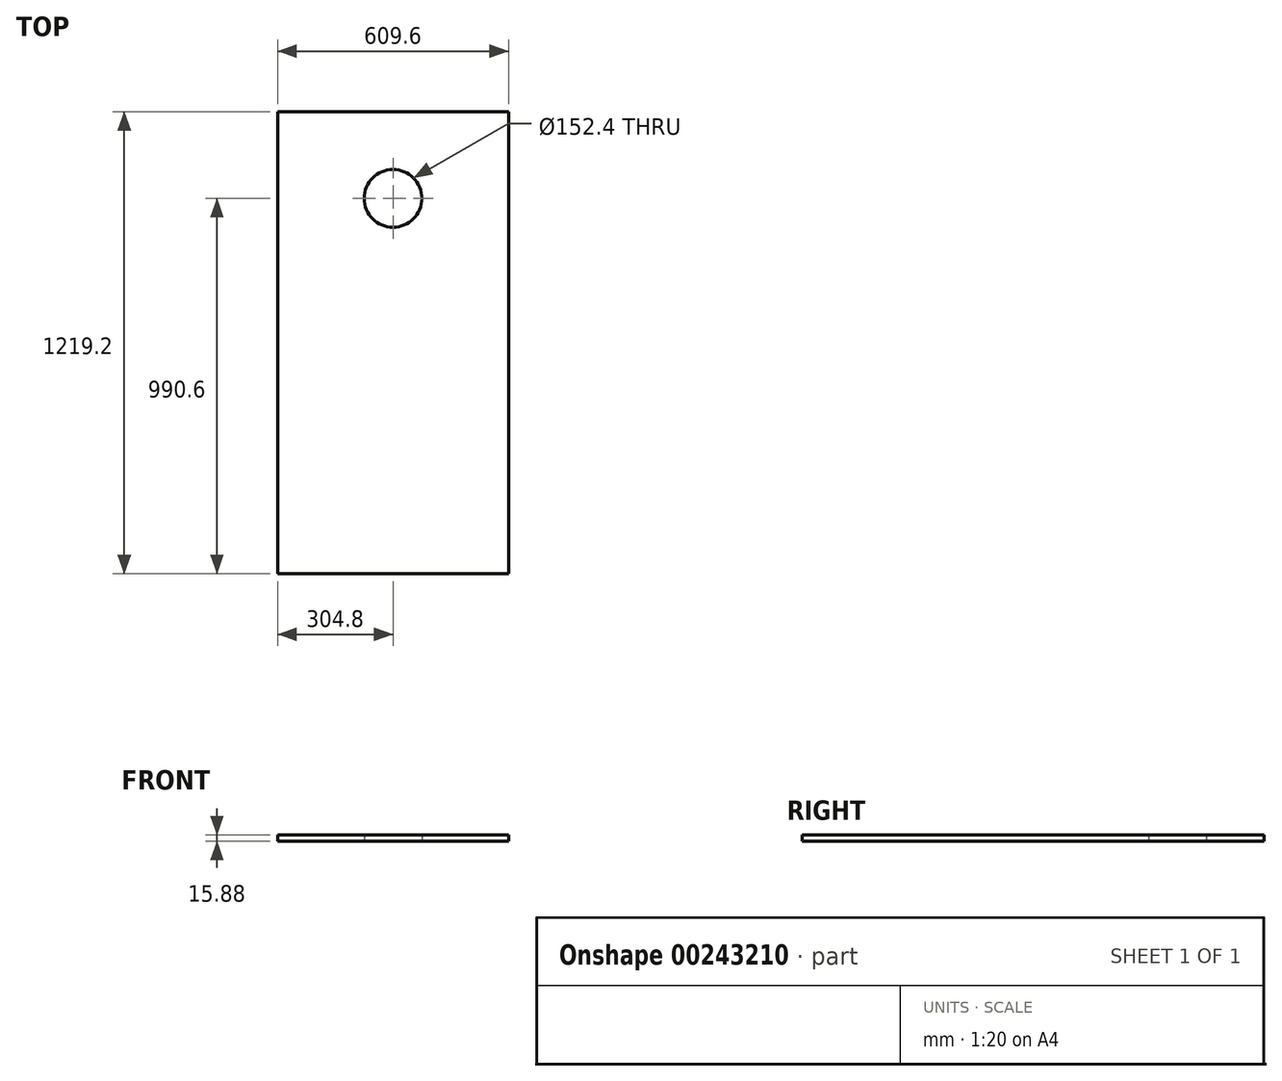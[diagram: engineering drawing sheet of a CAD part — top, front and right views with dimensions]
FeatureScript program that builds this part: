
annotation { "Feature Type Name" : "Feature", "Feature Type Description" : "" }
export const myFeature = defineFeature(function(context is Context, id is Id, definition is map)
    precondition{}
    {
        {
            var Q0;
            Q0=qCreatedBy(makeId("Top.planeOp"),FACE);
            var sketch = newSketch(context, id + "F0", { "sketchPlane" : qUnion([Q0])});
            skLineSegment(sketch, "E0.bottom", {"start": v(304.8, -609.6) * mm, "end": v(-304.8, -609.6) * mm});
            skLineSegment(sketch, "E0.top", {"start": v(304.8, 609.6) * mm, "end": v(-304.8, 609.6) * mm});
            skLineSegment(sketch, "E0.left", {"start": v(304.8, -609.6) * mm, "end": v(304.8, 609.6) * mm});
            skLineSegment(sketch, "E0.right", {"start": v(-304.8, -609.6) * mm, "end": v(-304.8, 609.6) * mm});
            skPoint(sketch, "E0.middle", {"position": v(0, 0) * mm});
            skCircle(sketch, "E1", {"center": v(0, 381) * mm, "radius": 76.2 * mm});
            skSolve(sketch);
        }
        {
            var Q0;
            Q0 = qSketchRegion(id + "F0", true);
            extrude(context, id + "F1", {"entities" : qUnion([Q0]), "depth" : 15.88 * mm});
        }
    });
